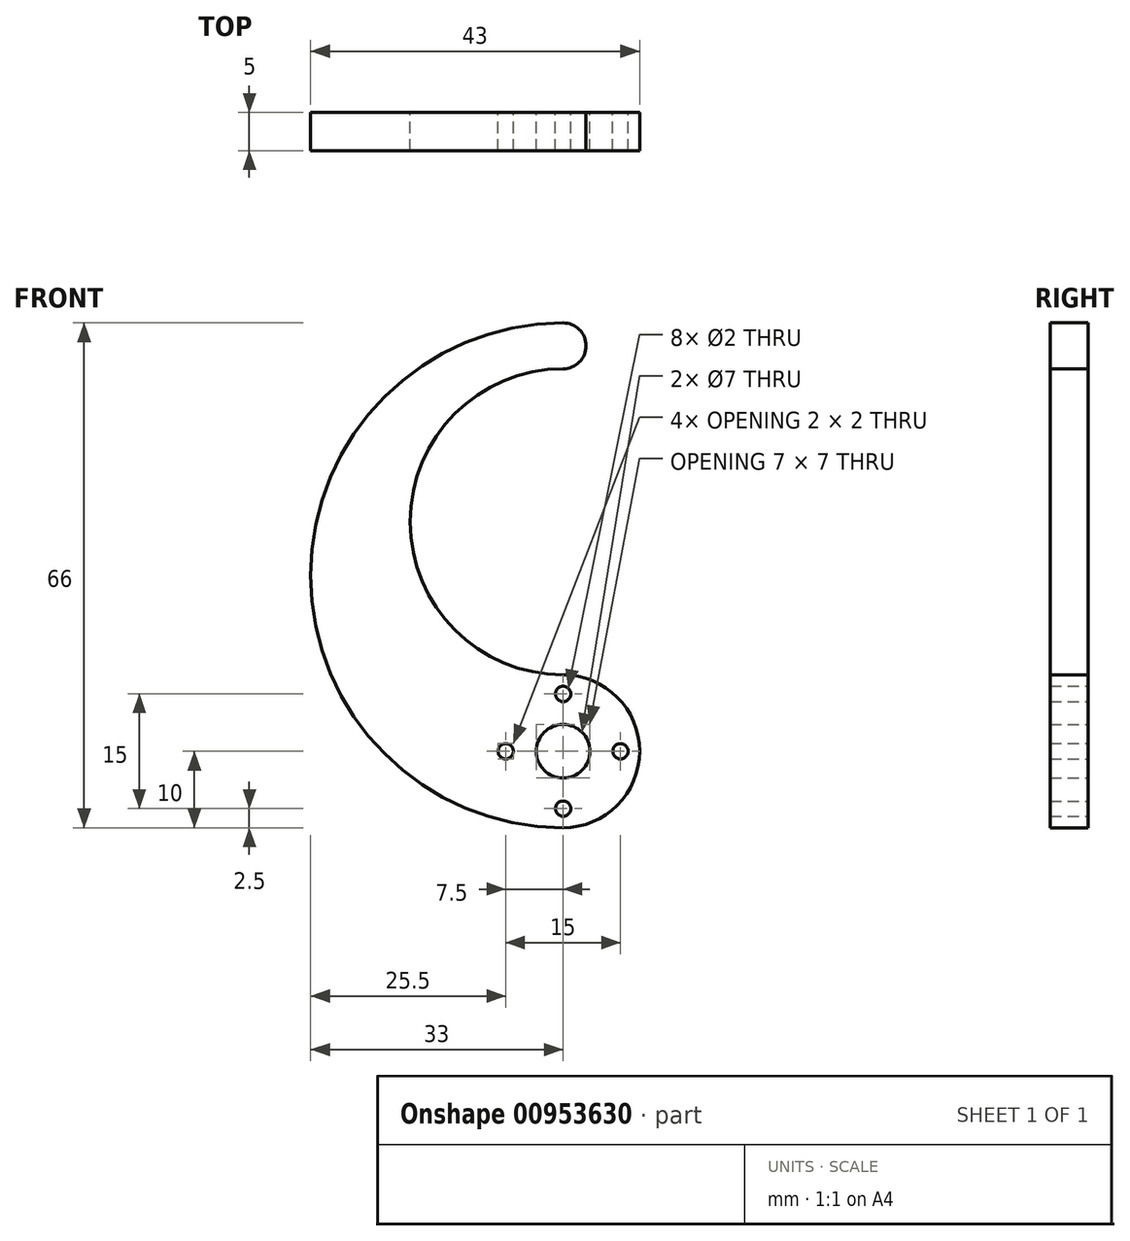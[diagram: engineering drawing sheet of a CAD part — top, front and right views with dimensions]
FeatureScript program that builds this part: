
annotation { "Feature Type Name" : "Feature", "Feature Type Description" : "" }
export const myFeature = defineFeature(function(context is Context, id is Id, definition is map)
    precondition{}
    {
        {
            var Q0;
            Q0=qCreatedBy(makeId("Front.planeOp"),FACE);
            var sketch = newSketch(context, id + "F0", { "sketchPlane" : qUnion([Q0])});
            skArc(sketch, "E0", {"start": v(0, -10) * mm, "mid": v(10, 0) * mm, "end": v(0, 10) * mm});
            skArc(sketch, "E1", {"start": v(0, 50) * mm, "mid": v(-20, 30) * mm, "end": v(0, 10) * mm});
            skArc(sketch, "E2", {"start": v(0, 50) * mm, "mid": v(3, 53) * mm, "end": v(0, 56) * mm});
            skArc(sketch, "E3", {"start": v(0, 56) * mm, "mid": v(-33, 23) * mm, "end": v(0, -10) * mm});
            skCircle(sketch, "E4", {"center": v(0, 0) * mm, "radius": 7.5 * mm, "construction": true});
            skLineSegment(sketch, "E5", {"start": v(0, 70.55) * mm, "end": v(0, -32.72) * mm, "construction": true});
            skLineSegment(sketch, "E6", {"start": v(-43.72, 0) * mm, "end": v(49.5, 0) * mm, "construction": true});
            skLineSegment(sketch, "E7", {"start": v(-6.66, 53) * mm, "end": v(14, 53) * mm, "construction": true});
            skPoint(sketch, "E8", {"position": v(0, 7.5) * mm});
            skPoint(sketch, "E9", {"position": v(7.5, 0) * mm});
            skPoint(sketch, "E10", {"position": v(0, -7.5) * mm});
            skPoint(sketch, "E11", {"position": v(-7.5, 0) * mm});
            skSolve(sketch);
        }
        {
            var Q0;
            Q0=makeQuery(id+"F0.imprint","IMPRINT",FACE,{"disambiguationData":[TD([[makeQuery(id+"F0.imprint","IMPRINT",EDGE,{"derivedFrom":sQuery(id+"F0.wireOp",EDGE,"E0")}),1.0]])]});
            extrude(context, id + "F1", {"entities" : qUnion([Q0]), "depth" : 5 * mm, "offsetDistance" : 25 * mm});
        }
        {
            var Q0;
            Q0=sQuery(id+"F0.wireOp",VERTEX,"E0.center");
            var Q1;
            Q1=makeQuery(id+"F1.opExtrude","SWEPT_BODY",BODY,{"disambiguationData":[OSD([sQuery(id+"F0.wireOp",EDGE,"E0"),sQuery(id+"F0.wireOp",EDGE,"E1"),sQuery(id+"F0.wireOp",EDGE,"E2"),sQuery(id+"F0.wireOp",EDGE,"E3")])]});
            hole(context, id + "F2", {"style" : HoleStyle.SIMPLE, "endStyle" : HoleEndStyle.THROUGH, "oppositeDirection" : true, "holeDiameter" : 7 * mm, "majorDiameter" : 5 * mm, "isTappedThrough" : true, "tappedDepth" : 12 * mm, "tapClearance" : 3, "locations" : qUnion([Q0]), "scope" : qUnion([Q1])});
        }
        {
            var Q0;
            Q0=sQuery(id+"F0.wireOp",VERTEX,"E8");
            var Q1;
            Q1=sQuery(id+"F0.wireOp",VERTEX,"E9");
            var Q2;
            Q2=sQuery(id+"F0.wireOp",VERTEX,"E10");
            var Q3;
            Q3=sQuery(id+"F0.wireOp",VERTEX,"E11");
            var Q4;
            Q4=makeQuery(id+"F1.opExtrude","SWEPT_BODY",BODY,{"disambiguationData":[OSD([sQuery(id+"F0.wireOp",EDGE,"E0"),sQuery(id+"F0.wireOp",EDGE,"E1"),sQuery(id+"F0.wireOp",EDGE,"E2"),sQuery(id+"F0.wireOp",EDGE,"E3")])]});
            hole(context, id + "F3", {"style" : HoleStyle.SIMPLE, "endStyle" : HoleEndStyle.THROUGH, "oppositeDirection" : true, "holeDiameter" : 2 * mm, "majorDiameter" : 5 * mm, "isTappedThrough" : true, "tappedDepth" : 12 * mm, "tapClearance" : 3, "locations" : qUnion([Q0, Q1, Q2, Q3]), "scope" : qUnion([Q4])});
        }
    });
